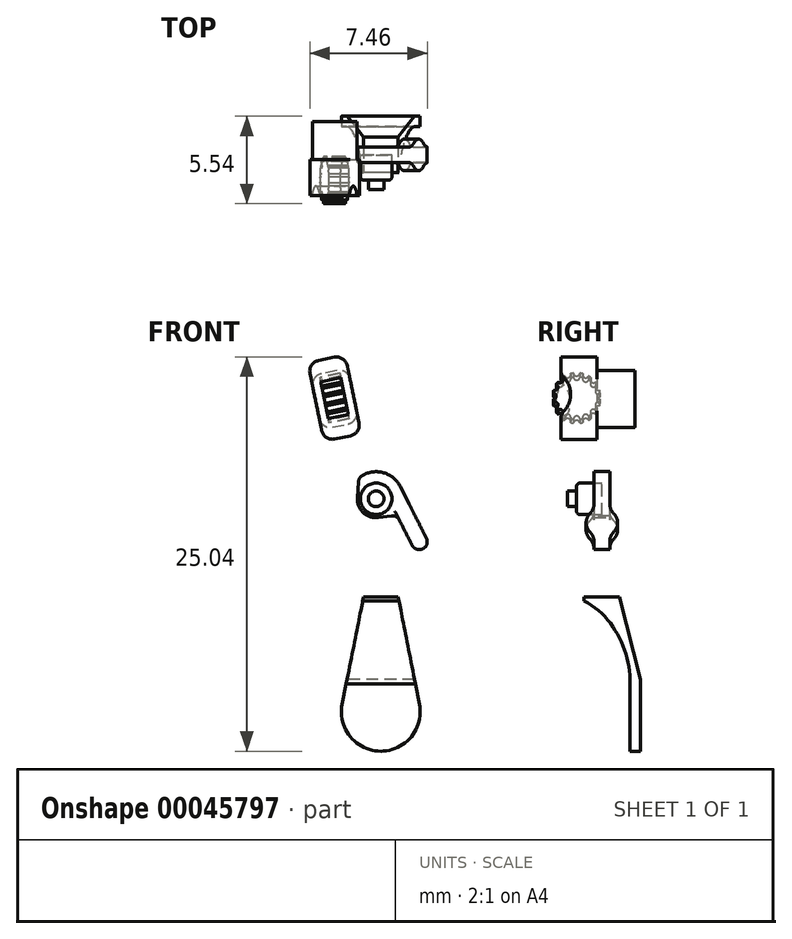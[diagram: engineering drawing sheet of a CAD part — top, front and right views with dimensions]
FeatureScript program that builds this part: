
annotation { "Feature Type Name" : "Feature", "Feature Type Description" : "" }
export const myFeature = defineFeature(function(context is Context, id is Id, definition is map)
    precondition{}
    {
        {
            var Q0;
            Q0=qCreatedBy(makeId("Front.planeOp"),FACE);
            var sketch = newSketch(context, id + "F0", { "sketchPlane" : qUnion([Q0])});
            skLineSegment(sketch, "E0", {"start": v(0, 0) * mm, "end": v(0, 60) * mm, "construction": true});
            skPoint(sketch, "E1", {"position": v(0, 45.67) * mm});
            skPoint(sketch, "E2", {"position": v(0, 38.34) * mm});
            skFitSpline(sketch, "E3", {"points": [v(0, 60) * mm, v(-1.86, 59.64) * mm, v(-3.72, 58.63) * mm, v(-4.74, 57.34) * mm, v(-5.39, 55.57) * mm, v(-5.56, 53.79) * mm, v(-5.4, 52.66) * mm, v(-4.8, 51.28) * mm, v(-3.8, 50.28) * mm, v(-2.1, 49.44) * mm, v(-0.7, 49.05) * mm, v(0, 48.98) * mm], "startDerivative": vector(-14.98, 0) * mm, "endDerivative": vector(13.56, 0) * mm});
            skFitSpline(sketch, "E4", {"points": [v(0, 58.38) * mm, v(-1.4, 58.1) * mm, v(-2.66, 57.4) * mm, v(-3.42, 56.4) * mm, v(-3.86, 54.9) * mm, v(-3.96, 53.33) * mm, v(-3.62, 52.35) * mm, v(-2.77, 51.4) * mm, v(-1.5, 50.78) * mm, v(0, 50.55) * mm], "startDerivative": vector(-10.6, 0) * mm, "endDerivative": vector(9.12, 0) * mm});
            skSolve(sketch);
        }
        {
            var Q0;
            Q0=qCreatedBy(makeId("Top.planeOp"),FACE);
            var Q1;
            Q1=sQuery(id+"F0.wireOp",VERTEX,"E1");
            cPlane(context, id + "F1", {"entities" : qUnion([Q0, Q1]), "cplaneType" : CPlaneType.PLANE_POINT, "offset" : 150 * mm, "width" : 150 * mm, "height" : 150 * mm});
        }
        {
            var Q0;
            Q0=qCreatedBy(id+"F1.planeOp",FACE);
            var sketch = newSketch(context, id + "F2", { "sketchPlane" : qUnion([Q0])});
            skCircle(sketch, "E5", {"center": v(0, 0) * mm, "radius": 1.5 * mm});
            skSolve(sketch);
        }
        {
            var Q0;
            Q0 = qSketchRegion(id + "F2", true);
            extrude(context, id + "F3", {"entities" : qUnion([Q0]), "depth" : 4 * mm});
        }
        {
            var Q0;
            Q0=qCreatedBy(makeId("Right.planeOp"),FACE);
            var sketch = newSketch(context, id + "F4", { "sketchPlane" : qUnion([Q0])});
            skCircle(sketch, "E6", {"center": v(0, 49.76) * mm, "radius": 0.78 * mm});
            skCircle(sketch, "E7", {"center": v(0, 59.2) * mm, "radius": 0.8 * mm});
            skSolve(sketch);
        }
        {
            var Q1;
            Q1=makeQuery(id+"F4.imprint","IMPRINT",FACE,{"disambiguationData":[TD([[makeQuery(id+"F4.imprint","IMPRINT",EDGE,{"derivedFrom":sQuery(id+"F4.wireOp",EDGE,"E7")}),1.0]])]});
            var Q2;
            Q2=makeQuery(id+"F4.imprint","IMPRINT",FACE,{"disambiguationData":[TD([[makeQuery(id+"F4.imprint","IMPRINT",EDGE,{"derivedFrom":sQuery(id+"F4.wireOp",EDGE,"E6")}),1.0]])]});
            var Q3;
            Q3=sQuery(id+"F0.wireOp",EDGE,"E3");
            var Q4;
            Q4=sQuery(id+"F0.wireOp",EDGE,"E4");
            loft(context, id + "F5", {"operationType" : NewBodyOperationType.ADD, "addGuides" : true, "sheetProfilesArray" : [{ "sheetProfileEntities" : qUnion([Q1]) }, { "sheetProfileEntities" : qUnion([Q2]) }], "guidesArray" : [{ "guideEntities" : qUnion([Q3]), "guideDerivativeType" : LoftGuideDerivativeType.DEFAULT, "guideDerivativeMagnitude" : 1 }, { "guideEntities" : qUnion([Q4]), "guideDerivativeType" : LoftGuideDerivativeType.DEFAULT, "guideDerivativeMagnitude" : 1 }]});
        }
        {
            var Q0;
            Q0=makeQuery(id+"F3.opExtrude","SWEPT_BODY",BODY,{"disambiguationData":[OSD([sQuery(id+"F2.wireOp",EDGE,"E5")])]});
            var Q1;
            Q1=qCreatedBy(makeId("Right.planeOp"),FACE);
            mirror(context, id + "F6", {"operationType" : NewBodyOperationType.ADD, "entities" : qUnion([Q0]), "mirrorPlane" : qUnion([Q1])});
        }
        {
            var Q0;
            Q0=makeQuery(id+"F5.boolean.opBoolean","INTERSECT",EDGE,{"disambiguationData":[OD(0.0)],"derivedFrom":[makeQuery(id+"F3.opExtrude","CAP_FACE",FACE,{"disambiguationData":[OSD([sQuery(id+"F2.wireOp",EDGE,"E5")])],"isStart":false}),makeQuery(id+"F5.opLoft","SWEPT_FACE",FACE,{"disambiguationData":[OSD([sQuery(id+"F0.wireOp",EDGE,"E3"),sQuery(id+"F0.wireOp",EDGE,"E4"),sQuery(id+"F4.wireOp",EDGE,"E6"),sQuery(id+"F4.wireOp",EDGE,"E7")])]})]});
            var Q1;
            Q1=makeQuery(id+"F6.opPattern","COPY",EDGE,{"derivedFrom":makeQuery(id+"F5.boolean.opBoolean","INTERSECT",EDGE,{"disambiguationData":[OD(0.0)],"derivedFrom":[makeQuery(id+"F3.opExtrude","CAP_FACE",FACE,{"disambiguationData":[OSD([sQuery(id+"F2.wireOp",EDGE,"E5")])],"isStart":false}),makeQuery(id+"F5.opLoft","SWEPT_FACE",FACE,{"disambiguationData":[OSD([sQuery(id+"F0.wireOp",EDGE,"E3"),sQuery(id+"F0.wireOp",EDGE,"E4"),sQuery(id+"F4.wireOp",EDGE,"E6"),sQuery(id+"F4.wireOp",EDGE,"E7")])]})]}),"instanceName":"1"});
            var Q2;
            Q2=makeQuery(id+"F5.boolean.opBoolean","INTERSECT",EDGE,{"disambiguationData":[OD(1.0)],"derivedFrom":[makeQuery(id+"F3.opExtrude","CAP_FACE",FACE,{"disambiguationData":[OSD([sQuery(id+"F2.wireOp",EDGE,"E5")])],"isStart":false}),makeQuery(id+"F5.opLoft","SWEPT_FACE",FACE,{"disambiguationData":[OSD([sQuery(id+"F0.wireOp",EDGE,"E3"),sQuery(id+"F0.wireOp",EDGE,"E4"),sQuery(id+"F4.wireOp",EDGE,"E6"),sQuery(id+"F4.wireOp",EDGE,"E7")])]})]});
            var Q3;
            Q3=makeQuery(id+"F6.opPattern","COPY",EDGE,{"derivedFrom":makeQuery(id+"F5.boolean.opBoolean","INTERSECT",EDGE,{"disambiguationData":[OD(1.0)],"derivedFrom":[makeQuery(id+"F3.opExtrude","CAP_FACE",FACE,{"disambiguationData":[OSD([sQuery(id+"F2.wireOp",EDGE,"E5")])],"isStart":false}),makeQuery(id+"F5.opLoft","SWEPT_FACE",FACE,{"disambiguationData":[OSD([sQuery(id+"F0.wireOp",EDGE,"E3"),sQuery(id+"F0.wireOp",EDGE,"E4"),sQuery(id+"F4.wireOp",EDGE,"E6"),sQuery(id+"F4.wireOp",EDGE,"E7")])]})]}),"instanceName":"1"});
            var Q4;
            Q4=makeQuery(id+"F6.opPattern","COPY",EDGE,{"derivedFrom":makeQuery(id+"F5.boolean.opBoolean","INTERSECT",EDGE,{"derivedFrom":[makeQuery(id+"F3.opExtrude","SWEPT_FACE",FACE,{"disambiguationData":[OSD([sQuery(id+"F2.wireOp",EDGE,"E5")])]}),makeQuery(id+"F5.opLoft","SWEPT_FACE",FACE,{"disambiguationData":[OSD([sQuery(id+"F0.wireOp",EDGE,"E3"),sQuery(id+"F0.wireOp",EDGE,"E4"),sQuery(id+"F4.wireOp",EDGE,"E6"),sQuery(id+"F4.wireOp",EDGE,"E7")])]})]}),"instanceName":"1"});
            var Q5;
            Q5=makeQuery(id+"F5.boolean.opBoolean","INTERSECT",EDGE,{"derivedFrom":[makeQuery(id+"F3.opExtrude","SWEPT_FACE",FACE,{"disambiguationData":[OSD([sQuery(id+"F2.wireOp",EDGE,"E5")])]}),makeQuery(id+"F5.opLoft","SWEPT_FACE",FACE,{"disambiguationData":[OSD([sQuery(id+"F0.wireOp",EDGE,"E3"),sQuery(id+"F0.wireOp",EDGE,"E4"),sQuery(id+"F4.wireOp",EDGE,"E6"),sQuery(id+"F4.wireOp",EDGE,"E7")])]})]});
            fillet(context, id + "F7", {"entities" : qUnion([Q0, Q1, Q2, Q3, Q4, Q5]), "radius" : 0.8 * mm, "tangentPropagation" : true, "allowEdgeOverflow" : false});
        }
        {
            var Q0;
            Q0=qCreatedBy(makeId("Front.planeOp"),FACE);
            var sketch = newSketch(context, id + "F8", { "sketchPlane" : qUnion([Q0])});
            skLineSegment(sketch, "E8", {"start": v(1.1, 45.67) * mm, "end": v(2.45, 38.86) * mm});
            skCircle(sketch, "E9", {"center": v(0, 38.37) * mm, "radius": 2.5 * mm});
            skLineSegment(sketch, "E10.MirrorCS", {"start": v(-1.1, 45.67) * mm, "end": v(-2.45, 38.86) * mm});
            skLineSegment(sketch, "E11", {"start": v(-1.1, 45.67) * mm, "end": v(1.1, 45.67) * mm});
            skPoint(sketch, "E12", {"position": v(0, 35.87) * mm});
            skLineSegment(sketch, "E13", {"start": v(0, 35.87) * mm, "end": v(17.53, 35.87) * mm, "construction": true});
            skSolve(sketch);
        }
        {
            var Q0;
            Q0=qCreatedBy(makeId("Right.planeOp"),FACE);
            var sketch = newSketch(context, id + "F9", { "sketchPlane" : qUnion([Q0])});
            skLineSegment(sketch, "E14", {"start": v(-1.13, 45.67) * mm, "end": v(1.13, 45.67) * mm});
            skLineSegment(sketch, "E15", {"start": v(1.13, 45.67) * mm, "end": v(2.45, 40.44) * mm});
            skLineSegment(sketch, "E16", {"start": v(2.45, 40.44) * mm, "end": v(2.45, 35.87) * mm});
            skLineSegment(sketch, "E17", {"start": v(2.45, 35.87) * mm, "end": v(1.8, 35.87) * mm});
            skLineSegment(sketch, "E18", {"start": v(1.8, 35.87) * mm, "end": v(1.8, 40.15) * mm});
            skFitSpline(sketch, "E19", {"points": [v(1.8, 40.15) * mm, v(0.18, 44.44) * mm, v(-1.13, 45.42) * mm], "startDerivative": vector(0.15, 9.68) * mm, "endDerivative": vector(-4.73, 2.78) * mm});
            skLineSegment(sketch, "E20", {"start": v(-1.13, 45.67) * mm, "end": v(-1.13, 45.42) * mm});
            skSolve(sketch);
        }
        {
            var Q0;
            Q0 = qSketchRegion(id + "F9", true);
            extrude(context, id + "F10", {"entities" : qUnion([Q0]), "endBound" : BoundingType.SYMMETRIC, "depth" : 6 * mm});
        }
        {
            var Q0;
            {var subQ2=sQuery(id+"F8.wireOp",EDGE,"E8");Q0=makeQuery(id+"F8.imprint","IMPRINT",FACE,{"disambiguationData":[TD([[makeQuery(id+"F8.imprint","IMPRINT",EDGE,{"derivedFrom":subQ2}),-1.0]])]});}
            var Q1;
            {var subQ0=sQuery(id+"F8.wireOp",EDGE,"E9");var subQ2=makeQuery(id+"F8.imprint","INTERSECT",VERTEX,{"derivedFrom":[sQuery(id+"F8.wireOp",EDGE,"E8"),subQ0]});Q1=makeQuery(id+"F8.imprint","IMPRINT",FACE,{"disambiguationData":[TD([[makeQuery(id+"F8.imprint","IMPRINT",EDGE,{"disambiguationData":[TD([[subQ2,-1.0]])],"derivedFrom":subQ0}),1.0]])]});}
            extrude(context, id + "F11", {"entities" : qUnion([Q0, Q1]), "operationType" : NewBodyOperationType.INTERSECT, "endBound" : BoundingType.SYMMETRIC, "oppositeDirection" : true, "depth" : 25 * mm});
        }
        {
            var Q0;
            Q0=qCreatedBy(makeId("Front.planeOp"),FACE);
            var sketch = newSketch(context, id + "F12", { "sketchPlane" : qUnion([Q0])});
            skLineSegment(sketch, "E21", {"start": v(-4.64, 60.55) * mm, "end": v(-2.27, 61.04) * mm});
            skLineSegment(sketch, "E22", {"start": v(-2.27, 61.04) * mm, "end": v(-1.24, 56.04) * mm});
            skLineSegment(sketch, "E23", {"start": v(-1.24, 56.04) * mm, "end": v(-3.61, 55.56) * mm});
            skLineSegment(sketch, "E24", {"start": v(-4.64, 60.55) * mm, "end": v(-3.61, 55.56) * mm});
            skSolve(sketch);
        }
        {
            var Q0;
            Q0 = qSketchRegion(id + "F12", true);
            extrude(context, id + "F13", {"entities" : qUnion([Q0]), "depth" : 2.6 * mm, "hasSecondDirection" : true, "secondDirectionOppositeDirection" : false, "secondDirectionDepth" : 0.3 * mm});
        }
        {
            var Q0;
            Q0=makeQuery(id+"F13.opExtrude","SWEPT_FACE",FACE,{"disambiguationData":[OSD([sQuery(id+"F12.wireOp",EDGE,"E22")])]});
            var sketch = newSketch(context, id + "F14", { "sketchPlane" : qUnion([Q0])});
            skCircle(sketch, "E25", {"center": v(-3.58, 57.7) * mm, "radius": 1.6 * mm});
            skPoint(sketch, "E26", {"position": v(-2.6, 57.7) * mm});
            skSolve(sketch);
        }
        {
            var Q0;
            Q0 = qSketchRegion(id + "F14", true);
            var Q1;
            Q1=makeQuery(id+"F13.opExtrude","SWEPT_FACE",FACE,{"disambiguationData":[OSD([sQuery(id+"F12.wireOp",EDGE,"E24")])]});
            extrude(context, id + "F15", {"entities" : qUnion([Q0]), "operationType" : NewBodyOperationType.REMOVE, "endBound" : BoundingType.UP_TO_SURFACE, "oppositeDirection" : true, "endBoundEntityFace" : qUnion([Q1]), "depth" : 25 * mm});
        }
        {
            var Q0;
            Q0=makeQuery(id+"F13.opExtrude","CAP_FACE",FACE,{"disambiguationData":[OSD([sQuery(id+"F12.wireOp",EDGE,"E21"),sQuery(id+"F12.wireOp",EDGE,"E22"),sQuery(id+"F12.wireOp",EDGE,"E23"),sQuery(id+"F12.wireOp",EDGE,"E24")])],"isStart":true});
            var sketch = newSketch(context, id + "F16", { "sketchPlane" : qUnion([Q0])});
            skLineSegment(sketch, "E27", {"start": v(2.1, 60.2) * mm, "end": v(4.46, 59.7) * mm});
            skLineSegment(sketch, "E28", {"start": v(4.46, 59.7) * mm, "end": v(3.77, 56.31) * mm});
            skLineSegment(sketch, "E29", {"start": v(3.77, 56.31) * mm, "end": v(1.4, 56.8) * mm});
            skLineSegment(sketch, "E30", {"start": v(1.4, 56.8) * mm, "end": v(2.1, 60.2) * mm});
            skSolve(sketch);
        }
        {
            var Q0;
            Q0 = qSketchRegion(id + "F16", true);
            extrude(context, id + "F17", {"entities" : qUnion([Q0]), "operationType" : NewBodyOperationType.ADD, "depth" : 2.4 * mm});
        }
        {
            var Q0;
            Q0=makeQuery(id+"F17.opExtrude","SWEPT_EDGE",EDGE,{"disambiguationData":[OSD([sQuery(id+"F12.wireOp",EDGE,"E24"),sQuery(id+"F16.wireOp",EDGE,"E27"),sQuery(id+"F16.wireOp",EDGE,"E28")])]});
            var Q1;
            Q1=makeQuery(id+"F13.opExtrude","SWEPT_EDGE",EDGE,{"disambiguationData":[OSD([sQuery(id+"F12.wireOp",EDGE,"E21"),sQuery(id+"F12.wireOp",EDGE,"E24")])]});
            var Q2;
            Q2=makeQuery(id+"F17.opExtrude","SWEPT_EDGE",EDGE,{"disambiguationData":[OSD([sQuery(id+"F12.wireOp",EDGE,"E22"),sQuery(id+"F16.wireOp",EDGE,"E27"),sQuery(id+"F16.wireOp",EDGE,"E30")])]});
            var Q3;
            Q3=makeQuery(id+"F13.opExtrude","SWEPT_EDGE",EDGE,{"disambiguationData":[OSD([sQuery(id+"F12.wireOp",EDGE,"E21"),sQuery(id+"F12.wireOp",EDGE,"E22")])]});
            var Q4;
            Q4=makeQuery(id+"F17.opExtrude","SWEPT_EDGE",EDGE,{"disambiguationData":[OSD([sQuery(id+"F12.wireOp",EDGE,"E24"),sQuery(id+"F16.wireOp",EDGE,"E28"),sQuery(id+"F16.wireOp",EDGE,"E29")])]});
            var Q5;
            Q5=makeQuery(id+"F13.opExtrude","SWEPT_EDGE",EDGE,{"disambiguationData":[OSD([sQuery(id+"F12.wireOp",EDGE,"E23"),sQuery(id+"F12.wireOp",EDGE,"E24")])]});
            var Q6;
            Q6=makeQuery(id+"F13.opExtrude","SWEPT_EDGE",EDGE,{"disambiguationData":[OSD([sQuery(id+"F12.wireOp",EDGE,"E22"),sQuery(id+"F12.wireOp",EDGE,"E23")])]});
            var Q7;
            Q7=makeQuery(id+"F17.opExtrude","SWEPT_EDGE",EDGE,{"disambiguationData":[OSD([sQuery(id+"F12.wireOp",EDGE,"E22"),sQuery(id+"F16.wireOp",EDGE,"E29"),sQuery(id+"F16.wireOp",EDGE,"E30")])]});
            var Q8;
            Q8=makeQuery(id+"F15.boolean.opBoolean","INTERSECT",EDGE,{"disambiguationData":[OD(0.0)],"derivedFrom":[makeQuery(id+"F13.opExtrude","CAP_FACE",FACE,{"disambiguationData":[OSD([sQuery(id+"F12.wireOp",EDGE,"E21"),sQuery(id+"F12.wireOp",EDGE,"E22"),sQuery(id+"F12.wireOp",EDGE,"E23"),sQuery(id+"F12.wireOp",EDGE,"E24")])],"isStart":false}),makeQuery(id+"F15.opExtrude","SWEPT_FACE",FACE,{"disambiguationData":[OSD([sQuery(id+"F14.wireOp",EDGE,"E25")])]})]});
            var Q9;
            Q9=makeQuery(id+"F15.boolean.opBoolean","INTERSECT",EDGE,{"disambiguationData":[OD(1.0)],"derivedFrom":[makeQuery(id+"F13.opExtrude","CAP_FACE",FACE,{"disambiguationData":[OSD([sQuery(id+"F12.wireOp",EDGE,"E21"),sQuery(id+"F12.wireOp",EDGE,"E22"),sQuery(id+"F12.wireOp",EDGE,"E23"),sQuery(id+"F12.wireOp",EDGE,"E24")])],"isStart":false}),makeQuery(id+"F15.opExtrude","SWEPT_FACE",FACE,{"disambiguationData":[OSD([sQuery(id+"F14.wireOp",EDGE,"E25")])]})]});
            fillet(context, id + "F18", {"entities" : qUnion([Q0, Q1, Q2, Q3, Q4, Q5, Q6, Q7, Q8, Q9]), "radius" : 0.7 * mm, "tangentPropagation" : true, "allowEdgeOverflow" : false});
        }
        {
            var Q0;
            Q0=makeQuery(id+"F17.boolean.opBoolean","MERGE",FACE,{"derivedFrom":[makeQuery(id+"F13.opExtrude","SWEPT_FACE",FACE,{"disambiguationData":[OSD([sQuery(id+"F12.wireOp",EDGE,"E22")])]}),makeQuery(id+"F17.opExtrude","SWEPT_FACE",FACE,{"disambiguationData":[OSD([sQuery(id+"F16.wireOp",EDGE,"E30")])]})]});
            var Q1;
            Q1=makeQuery(id+"F17.boolean.opBoolean","MERGE",FACE,{"derivedFrom":[makeQuery(id+"F13.opExtrude","SWEPT_FACE",FACE,{"disambiguationData":[OSD([sQuery(id+"F12.wireOp",EDGE,"E24")])]}),makeQuery(id+"F17.opExtrude","SWEPT_FACE",FACE,{"disambiguationData":[OSD([sQuery(id+"F16.wireOp",EDGE,"E28")])]})]});
            cPlane(context, id + "F19", {"entities" : qUnion([Q0, Q1]), "cplaneType" : CPlaneType.MID_PLANE, "offset" : 150 * mm, "width" : 150 * mm, "height" : 150 * mm});
        }
        {
            var Q0;
            Q0=qCreatedBy(id+"F19.planeOp",FACE);
            var sketch = newSketch(context, id + "F20", { "sketchPlane" : qUnion([Q0])});
            skCircle(sketch, "E31", {"center": v(-1.6, 57.7) * mm, "radius": 1.5 * mm});
            skPoint(sketch, "E32.0", {"position": v(-2.6, 59.27) * mm});
            skPoint(sketch, "E33.0", {"position": v(-2.6, 56.13) * mm});
            skLineSegment(sketch, "E34", {"start": v(-2.6, 59.27) * mm, "end": v(-2.6, 56.13) * mm, "construction": true});
            skPoint(sketch, "E35", {"position": v(-2.6, 57.7) * mm});
            skCircle(sketch, "E36", {"center": v(-3.1, 57.7) * mm, "radius": 0.2 * mm});
            skCircle(sketch, "E37.1.0", {"center": v(-2.99, 57.12) * mm, "radius": 0.2 * mm});
            skCircle(sketch, "E37.2.0", {"center": v(-2.66, 56.64) * mm, "radius": 0.2 * mm});
            skCircle(sketch, "E37.3.0", {"center": v(-2.17, 56.31) * mm, "radius": 0.2 * mm});
            skCircle(sketch, "E37.4.0", {"center": v(-1.6, 56.2) * mm, "radius": 0.2 * mm});
            skCircle(sketch, "E37.5.0", {"center": v(-1.03, 56.31) * mm, "radius": 0.2 * mm});
            skCircle(sketch, "E37.6.0", {"center": v(-0.54, 56.64) * mm, "radius": 0.2 * mm});
            skCircle(sketch, "E37.7.0", {"center": v(-0.21, 57.12) * mm, "radius": 0.2 * mm});
            skCircle(sketch, "E37.8.0", {"center": v(-0.1, 57.7) * mm, "radius": 0.2 * mm});
            skCircle(sketch, "E37.9.0", {"center": v(-0.21, 58.27) * mm, "radius": 0.2 * mm});
            skCircle(sketch, "E37.10.0", {"center": v(-0.54, 58.76) * mm, "radius": 0.2 * mm});
            skCircle(sketch, "E37.11.0", {"center": v(-1.03, 59.08) * mm, "radius": 0.2 * mm});
            skCircle(sketch, "E37.12.0", {"center": v(-1.6, 59.2) * mm, "radius": 0.2 * mm});
            skCircle(sketch, "E37.13.0", {"center": v(-2.17, 59.08) * mm, "radius": 0.2 * mm});
            skCircle(sketch, "E37.14.0", {"center": v(-2.66, 58.76) * mm, "radius": 0.2 * mm});
            skCircle(sketch, "E37.15.0", {"center": v(-2.99, 58.27) * mm, "radius": 0.2 * mm});
            skSolve(sketch);
        }
        {
            var Q0;
            {var subQ1=sQuery(id+"F20.wireOp",EDGE,"E31");var subQ29=sQuery(id+"F20.wireOp",EDGE,"E37.9.0");var subQ31=makeQuery(id+"F20.imprint","INTERSECT",VERTEX,{"disambiguationData":[OD(0.0)],"derivedFrom":[subQ1,subQ29]});Q0=makeQuery(id+"F20.imprint","IMPRINT",FACE,{"disambiguationData":[TD([[makeQuery(id+"F20.imprint","IMPRINT",EDGE,{"disambiguationData":[TD([[subQ31,1.0]])],"derivedFrom":subQ1}),1.0]])]});}
            extrude(context, id + "F21", {"entities" : qUnion([Q0]), "endBound" : BoundingType.SYMMETRIC, "depth" : 1.3 * mm});
        }
        {
            var Q0;
            Q0=qCreatedBy(makeId("Front.planeOp"),FACE);
            var sketch = newSketch(context, id + "F22", { "sketchPlane" : qUnion([Q0])});
            skCircle(sketch, "E38", {"center": v(-0.3, 51.9) * mm, "radius": 1 * mm});
            skSolve(sketch);
        }
        {
            var Q0;
            Q0=makeQuery(id+"F22.imprint","IMPRINT",FACE,{"disambiguationData":[TD([[makeQuery(id+"F22.imprint","IMPRINT",EDGE,{"derivedFrom":sQuery(id+"F22.wireOp",EDGE,"E38")}),1.0]])]});
            extrude(context, id + "F23", {"entities" : qUnion([Q0]), "depth" : 1.6 * mm});
        }
        {
            var Q0;
            Q0=makeQuery(id+"F23.opExtrude","CAP_FACE",FACE,{"disambiguationData":[OSD([sQuery(id+"F22.wireOp",EDGE,"E38")])],"isStart":false});
            var sketch = newSketch(context, id + "F24", { "sketchPlane" : qUnion([Q0])});
            skCircle(sketch, "E39", {"center": v(-0.3, 51.9) * mm, "radius": 0.5 * mm});
            skSolve(sketch);
        }
        {
            var Q0;
            Q0=makeQuery(id+"F24.imprint","IMPRINT",FACE,{"disambiguationData":[TD([[makeQuery(id+"F24.imprint","IMPRINT",EDGE,{"derivedFrom":sQuery(id+"F24.wireOp",EDGE,"E39")}),1.0]])]});
            extrude(context, id + "F25", {"entities" : qUnion([Q0]), "operationType" : NewBodyOperationType.ADD, "depth" : 0.6 * mm});
        }
        {
            var Q0;
            Q0=qCreatedBy(makeId("Front.planeOp"),FACE);
            var sketch = newSketch(context, id + "F26", { "sketchPlane" : qUnion([Q0])});
            skLineSegment(sketch, "E40", {"start": v(1.24, 52.68) * mm, "end": v(3.12, 48.96) * mm});
            skLineSegment(sketch, "E41", {"start": v(3.12, 48.96) * mm, "end": v(2.22, 48.5) * mm});
            skLineSegment(sketch, "E42", {"start": v(2.22, 48.5) * mm, "end": v(1.02, 50.87) * mm});
            skLineSegment(sketch, "E43", {"start": v(1.02, 50.87) * mm, "end": v(-0.13, 50.71) * mm});
            skArc(sketch, "E44", {"start": v(1.24, 52.68) * mm, "mid": v(0.05, 53.59) * mm, "end": v(-1.4, 53.22) * mm});
            skArc(sketch, "E45", {"start": v(-1.5, 51.99) * mm, "mid": v(-1.12, 51.03) * mm, "end": v(-0.13, 50.71) * mm});
            skLineSegment(sketch, "E46", {"start": v(-1.5, 51.99) * mm, "end": v(-1.4, 53.22) * mm});
            skSolve(sketch);
        }
        {
            var Q0;
            Q0 = qSketchRegion(id + "F26", true);
            extrude(context, id + "F27", {"entities" : qUnion([Q0]), "endBound" : BoundingType.SYMMETRIC, "depth" : 1 * mm});
        }
        {
            var Q0;
            Q0=makeQuery(id+"F27.opExtrude","SWEPT_EDGE",EDGE,{"disambiguationData":[OSD([sQuery(id+"F26.wireOp",EDGE,"E40"),sQuery(id+"F26.wireOp",EDGE,"E41")])]});
            var Q1;
            Q1=makeQuery(id+"F27.opExtrude","SWEPT_EDGE",EDGE,{"disambiguationData":[OSD([sQuery(id+"F26.wireOp",EDGE,"E41"),sQuery(id+"F26.wireOp",EDGE,"E42")])]});
            var Q2;
            Q2=makeQuery(id+"F27.opExtrude","SWEPT_EDGE",EDGE,{"disambiguationData":[OSD([sQuery(id+"F26.wireOp",EDGE,"E44"),sQuery(id+"F26.wireOp",EDGE,"E46")])]});
            var Q3;
            Q3=makeQuery(id+"F27.opExtrude","SWEPT_EDGE",EDGE,{"disambiguationData":[OSD([sQuery(id+"F26.wireOp",EDGE,"E42"),sQuery(id+"F26.wireOp",EDGE,"E43")])]});
            fillet(context, id + "F28", {"entities" : qUnion([Q0, Q1, Q2, Q3]), "radius" : 0.5 * mm, "tangentPropagation" : true, "allowEdgeOverflow" : false});
        }
        {
            var Q0;
            Q0=makeQuery(id+"F23.opExtrude","CAP_EDGE",EDGE,{"disambiguationData":[OSD([sQuery(id+"F22.wireOp",EDGE,"E38")])],"isStart":false});
            fillet(context, id + "F29", {"entities" : qUnion([Q0]), "radius" : 0.2 * mm, "tangentPropagation" : true, "allowEdgeOverflow" : false});
        }
        {
            var Q0;
            Q0=makeQuery(id+"F27.opExtrude","SWEPT_FACE",FACE,{"disambiguationData":[OSD([sQuery(id+"F26.wireOp",EDGE,"E40")])]});
            var sketch = newSketch(context, id + "F30", { "sketchPlane" : qUnion([Q0])});
            skLineSegment(sketch, "E47.0", {"start": v(-0.5, 42.81) * mm, "end": v(0.5, 42.81) * mm, "construction": true});
            skPoint(sketch, "E48", {"position": v(0, 42.81) * mm});
            skLineSegment(sketch, "E49", {"start": v(0, 42.81) * mm, "end": v(0, 45.01) * mm, "construction": true});
            skCircle(sketch, "E50", {"center": v(0, 43.91) * mm, "radius": 1 * mm});
            skSolve(sketch);
        }
        {
            var Q0;
            Q0 = qSketchRegion(id + "F30", true);
            var Q1;
            Q1=makeQuery(id+"F27.opExtrude","SWEPT_FACE",FACE,{"disambiguationData":[OSD([sQuery(id+"F26.wireOp",EDGE,"E42")])]});
            extrude(context, id + "F31", {"entities" : qUnion([Q0]), "operationType" : NewBodyOperationType.ADD, "endBound" : BoundingType.UP_TO_SURFACE, "oppositeDirection" : true, "endBoundEntityFace" : qUnion([Q1]), "depth" : 25 * mm});
        }
        {
            var Q0;
            Q0=makeQuery(id+"F31.boolean.opBoolean","INTERSECT",EDGE,{"disambiguationData":[OD(0.0)],"derivedFrom":[makeQuery(id+"F27.opExtrude","CAP_FACE",FACE,{"disambiguationData":[OSD([sQuery(id+"F26.wireOp",EDGE,"E40"),sQuery(id+"F26.wireOp",EDGE,"E41"),sQuery(id+"F26.wireOp",EDGE,"E42"),sQuery(id+"F26.wireOp",EDGE,"E43"),sQuery(id+"F26.wireOp",EDGE,"E44"),sQuery(id+"F26.wireOp",EDGE,"E45"),sQuery(id+"F26.wireOp",EDGE,"E46")])],"isStart":false}),makeQuery(id+"F31.opExtrude","SWEPT_FACE",FACE,{"disambiguationData":[OSD([sQuery(id+"F30.wireOp",EDGE,"E50")])]})]});
            var Q1;
            Q1=makeQuery(id+"F31.boolean.opBoolean","INTERSECT",EDGE,{"disambiguationData":[OD(1.0)],"derivedFrom":[makeQuery(id+"F27.opExtrude","CAP_FACE",FACE,{"disambiguationData":[OSD([sQuery(id+"F26.wireOp",EDGE,"E40"),sQuery(id+"F26.wireOp",EDGE,"E41"),sQuery(id+"F26.wireOp",EDGE,"E42"),sQuery(id+"F26.wireOp",EDGE,"E43"),sQuery(id+"F26.wireOp",EDGE,"E44"),sQuery(id+"F26.wireOp",EDGE,"E45"),sQuery(id+"F26.wireOp",EDGE,"E46")])],"isStart":false}),makeQuery(id+"F31.opExtrude","SWEPT_FACE",FACE,{"disambiguationData":[OSD([sQuery(id+"F30.wireOp",EDGE,"E50")])]})]});
            var Q2;
            Q2=makeQuery(id+"F31.boolean.opBoolean","INTERSECT",EDGE,{"disambiguationData":[OD(0.0)],"derivedFrom":[makeQuery(id+"F27.opExtrude","CAP_FACE",FACE,{"disambiguationData":[OSD([sQuery(id+"F26.wireOp",EDGE,"E40"),sQuery(id+"F26.wireOp",EDGE,"E41"),sQuery(id+"F26.wireOp",EDGE,"E42"),sQuery(id+"F26.wireOp",EDGE,"E43"),sQuery(id+"F26.wireOp",EDGE,"E44"),sQuery(id+"F26.wireOp",EDGE,"E45"),sQuery(id+"F26.wireOp",EDGE,"E46")])],"isStart":true}),makeQuery(id+"F31.opExtrude","SWEPT_FACE",FACE,{"disambiguationData":[OSD([sQuery(id+"F30.wireOp",EDGE,"E50")])]})]});
            var Q3;
            Q3=makeQuery(id+"F31.boolean.opBoolean","INTERSECT",EDGE,{"disambiguationData":[OD(1.0)],"derivedFrom":[makeQuery(id+"F27.opExtrude","CAP_FACE",FACE,{"disambiguationData":[OSD([sQuery(id+"F26.wireOp",EDGE,"E40"),sQuery(id+"F26.wireOp",EDGE,"E41"),sQuery(id+"F26.wireOp",EDGE,"E42"),sQuery(id+"F26.wireOp",EDGE,"E43"),sQuery(id+"F26.wireOp",EDGE,"E44"),sQuery(id+"F26.wireOp",EDGE,"E45"),sQuery(id+"F26.wireOp",EDGE,"E46")])],"isStart":true}),makeQuery(id+"F31.opExtrude","SWEPT_FACE",FACE,{"disambiguationData":[OSD([sQuery(id+"F30.wireOp",EDGE,"E50")])]})]});
            fillet(context, id + "F32", {"entities" : qUnion([Q0, Q1, Q2, Q3]), "radius" : 1 * mm, "tangentPropagation" : true, "allowEdgeOverflow" : false});
        }
    });
